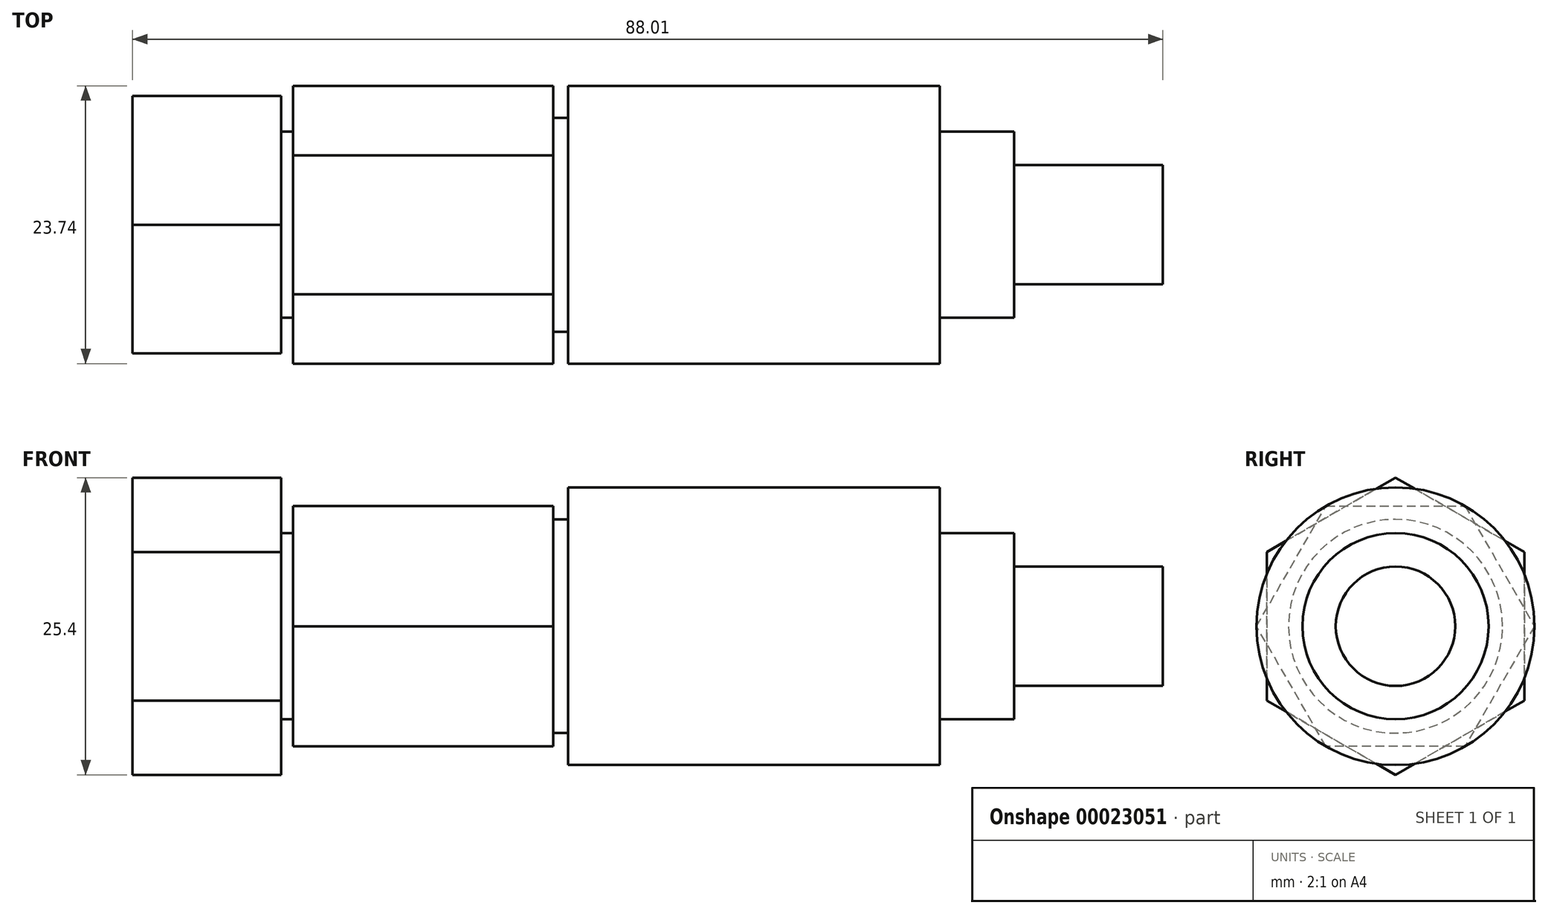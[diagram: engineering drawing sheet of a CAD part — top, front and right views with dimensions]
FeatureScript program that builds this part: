
annotation { "Feature Type Name" : "Feature", "Feature Type Description" : "" }
export const myFeature = defineFeature(function(context is Context, id is Id, definition is map)
    precondition{}
    {
        {
            var Q0;
            Q0=qCreatedBy(makeId("Front.planeOp"),FACE);
            var sketch = newSketch(context, id + "F0", { "sketchPlane" : qUnion([Q0])});
            skLineSegment(sketch, "E0", {"start": v(0, 0) * mm, "end": v(88.01, 0) * mm});
            skLineSegment(sketch, "E1", {"start": v(88.01, 0) * mm, "end": v(88.01, 5.1) * mm});
            skLineSegment(sketch, "E2", {"start": v(88.01, 5.1) * mm, "end": v(75.31, 5.1) * mm});
            skLineSegment(sketch, "E3", {"start": v(75.31, 5.1) * mm, "end": v(75.31, 7.95) * mm});
            skLineSegment(sketch, "E4", {"start": v(75.31, 7.95) * mm, "end": v(68.96, 7.95) * mm});
            skLineSegment(sketch, "E5", {"start": v(68.96, 7.95) * mm, "end": v(68.96, 11.87) * mm});
            skLineSegment(sketch, "E6", {"start": v(68.96, 11.87) * mm, "end": v(37.21, 11.87) * mm});
            skLineSegment(sketch, "E7", {"start": v(37.21, 11.87) * mm, "end": v(37.21, 9.14) * mm});
            skLineSegment(sketch, "E8", {"start": v(37.21, 9.14) * mm, "end": v(35.94, 9.14) * mm});
            skLineSegment(sketch, "E9", {"start": v(35.94, 9.14) * mm, "end": v(35.94, 11.87) * mm});
            skLineSegment(sketch, "E10", {"start": v(35.94, 11.87) * mm, "end": v(13.72, 11.87) * mm});
            skLineSegment(sketch, "E11", {"start": v(13.72, 11.87) * mm, "end": v(13.72, 7.95) * mm});
            skLineSegment(sketch, "E12", {"start": v(13.72, 7.95) * mm, "end": v(12.7, 7.95) * mm});
            skLineSegment(sketch, "E13", {"start": v(12.7, 7.95) * mm, "end": v(12.7, 12.7) * mm});
            skLineSegment(sketch, "E14", {"start": v(12.7, 12.7) * mm, "end": v(0, 12.7) * mm});
            skLineSegment(sketch, "E15", {"start": v(0, 12.7) * mm, "end": v(0, 0) * mm});
            skSolve(sketch);
        }
        {
            var Q0;
            Q0=makeQuery(id+"F0.imprint","IMPRINT",FACE,{"disambiguationData":[TD([[makeQuery(id+"F0.imprint","IMPRINT",EDGE,{"derivedFrom":sQuery(id+"F0.wireOp",EDGE,"E0")}),1.0]])]});
            var Q1;
            Q1=sQuery(id+"F0.wireOp",EDGE,"E0");
            revolve(context, id + "F1", {"entities" : qUnion([Q0]), "axis" : qUnion([Q1]), "revolveType" : RevolveType.FULL});
        }
        {
            var Q0;
            Q0=makeQuery(id+"F1.opRevolve","SWEPT_FACE",FACE,{"disambiguationData":[OSD([sQuery(id+"F0.wireOp",EDGE,"E15")])]});
            var sketch = newSketch(context, id + "F2", { "sketchPlane" : qUnion([Q0])});
            skCircle(sketch, "E16.cCircle", {"center": v(0, 0) * mm, "radius": 12.7 * mm, "construction": true});
            skLineSegment(sketch, "E16.0", {"start": v(0, 12.7) * mm, "end": v(11, 6.35) * mm});
            skLineSegment(sketch, "E16.1", {"start": v(11, 6.35) * mm, "end": v(11, -6.35) * mm});
            skLineSegment(sketch, "E16.2", {"start": v(11, -6.35) * mm, "end": v(0, -12.7) * mm});
            skLineSegment(sketch, "E16.3", {"start": v(0, -12.7) * mm, "end": v(-11, -6.35) * mm});
            skLineSegment(sketch, "E16.4", {"start": v(-11, -6.35) * mm, "end": v(-11, 6.35) * mm});
            skLineSegment(sketch, "E16.5", {"start": v(-11, 6.35) * mm, "end": v(0, 12.7) * mm});
            skSolve(sketch);
        }
        {
            var Q0;
            {var subQ1=sQuery(id+"F2.wireOp",EDGE,"E16.2");Q0=makeQuery(id+"F2.imprint","IMPRINT",FACE,{"disambiguationData":[TD([[makeQuery(id+"F2.imprint","IMPRINT",EDGE,{"derivedFrom":subQ1}),1.0]])]});}
            var Q1;
            {var subQ1=sQuery(id+"F2.wireOp",EDGE,"E16.1");Q1=makeQuery(id+"F2.imprint","IMPRINT",FACE,{"disambiguationData":[TD([[makeQuery(id+"F2.imprint","IMPRINT",EDGE,{"derivedFrom":subQ1}),1.0]])]});}
            var Q2;
            {var subQ1=sQuery(id+"F2.wireOp",EDGE,"E16.0");Q2=makeQuery(id+"F2.imprint","IMPRINT",FACE,{"disambiguationData":[TD([[makeQuery(id+"F2.imprint","IMPRINT",EDGE,{"derivedFrom":subQ1}),1.0]])]});}
            var Q3;
            {var subQ1=sQuery(id+"F2.wireOp",EDGE,"E16.5");Q3=makeQuery(id+"F2.imprint","IMPRINT",FACE,{"disambiguationData":[TD([[makeQuery(id+"F2.imprint","IMPRINT",EDGE,{"derivedFrom":subQ1}),1.0]])]});}
            var Q4;
            {var subQ1=sQuery(id+"F2.wireOp",EDGE,"E16.4");Q4=makeQuery(id+"F2.imprint","IMPRINT",FACE,{"disambiguationData":[TD([[makeQuery(id+"F2.imprint","IMPRINT",EDGE,{"derivedFrom":subQ1}),1.0]])]});}
            var Q5;
            {var subQ1=sQuery(id+"F2.wireOp",EDGE,"E16.3");Q5=makeQuery(id+"F2.imprint","IMPRINT",FACE,{"disambiguationData":[TD([[makeQuery(id+"F2.imprint","IMPRINT",EDGE,{"derivedFrom":subQ1}),1.0]])]});}
            var Q6;
            Q6=makeQuery(id+"F1.opRevolve","SWEPT_FACE",FACE,{"disambiguationData":[OSD([sQuery(id+"F0.wireOp",EDGE,"E13")])]});
            extrude(context, id + "F3", {"entities" : qUnion([Q0, Q1, Q2, Q3, Q4, Q5]), "operationType" : NewBodyOperationType.REMOVE, "endBound" : BoundingType.UP_TO_SURFACE, "oppositeDirection" : true, "endBoundEntityFace" : qUnion([Q6]), "depth" : 25.4 * mm});
        }
        {
            var Q0;
            Q0=makeQuery(id+"F1.opRevolve","SWEPT_FACE",FACE,{"disambiguationData":[OSD([sQuery(id+"F0.wireOp",EDGE,"E9")])]});
            var sketch = newSketch(context, id + "F4", { "sketchPlane" : qUnion([Q0])});
            skCircle(sketch, "E17.cCircle", {"center": v(0, 0) * mm, "radius": 11.87 * mm, "construction": true});
            skLineSegment(sketch, "E17.0", {"start": v(11.87, 0) * mm, "end": v(5.93, -10.28) * mm});
            skLineSegment(sketch, "E17.1", {"start": v(5.93, -10.28) * mm, "end": v(-5.93, -10.28) * mm});
            skLineSegment(sketch, "E17.2", {"start": v(-5.93, -10.28) * mm, "end": v(-11.87, 0) * mm});
            skLineSegment(sketch, "E17.3", {"start": v(-11.87, 0) * mm, "end": v(-5.93, 10.28) * mm});
            skLineSegment(sketch, "E17.4", {"start": v(-5.93, 10.28) * mm, "end": v(5.93, 10.28) * mm});
            skLineSegment(sketch, "E17.5", {"start": v(5.93, 10.28) * mm, "end": v(11.87, 0) * mm});
            skSolve(sketch);
        }
        {
            var Q0;
            {var subQ1=sQuery(id+"F4.wireOp",EDGE,"E17.3");Q0=makeQuery(id+"F4.imprint","IMPRINT",FACE,{"disambiguationData":[TD([[makeQuery(id+"F4.imprint","IMPRINT",EDGE,{"derivedFrom":subQ1}),1.0]])]});}
            var Q1;
            {var subQ1=sQuery(id+"F4.wireOp",EDGE,"E17.4");Q1=makeQuery(id+"F4.imprint","IMPRINT",FACE,{"disambiguationData":[TD([[makeQuery(id+"F4.imprint","IMPRINT",EDGE,{"derivedFrom":subQ1}),1.0]])]});}
            var Q2;
            {var subQ1=sQuery(id+"F4.wireOp",EDGE,"E17.2");Q2=makeQuery(id+"F4.imprint","IMPRINT",FACE,{"disambiguationData":[TD([[makeQuery(id+"F4.imprint","IMPRINT",EDGE,{"derivedFrom":subQ1}),1.0]])]});}
            var Q3;
            {var subQ1=sQuery(id+"F4.wireOp",EDGE,"E17.5");Q3=makeQuery(id+"F4.imprint","IMPRINT",FACE,{"disambiguationData":[TD([[makeQuery(id+"F4.imprint","IMPRINT",EDGE,{"derivedFrom":subQ1}),1.0]])]});}
            var Q4;
            {var subQ1=sQuery(id+"F4.wireOp",EDGE,"E17.0");Q4=makeQuery(id+"F4.imprint","IMPRINT",FACE,{"disambiguationData":[TD([[makeQuery(id+"F4.imprint","IMPRINT",EDGE,{"derivedFrom":subQ1}),1.0]])]});}
            var Q5;
            {var subQ1=sQuery(id+"F4.wireOp",EDGE,"E17.1");Q5=makeQuery(id+"F4.imprint","IMPRINT",FACE,{"disambiguationData":[TD([[makeQuery(id+"F4.imprint","IMPRINT",EDGE,{"derivedFrom":subQ1}),1.0]])]});}
            var Q6;
            Q6=makeQuery(id+"F1.opRevolve","SWEPT_FACE",FACE,{"disambiguationData":[OSD([sQuery(id+"F0.wireOp",EDGE,"E11")])]});
            extrude(context, id + "F5", {"entities" : qUnion([Q0, Q1, Q2, Q3, Q4, Q5]), "operationType" : NewBodyOperationType.REMOVE, "endBound" : BoundingType.UP_TO_SURFACE, "oppositeDirection" : true, "endBoundEntityFace" : qUnion([Q6]), "depth" : 25.4 * mm});
        }
    });
